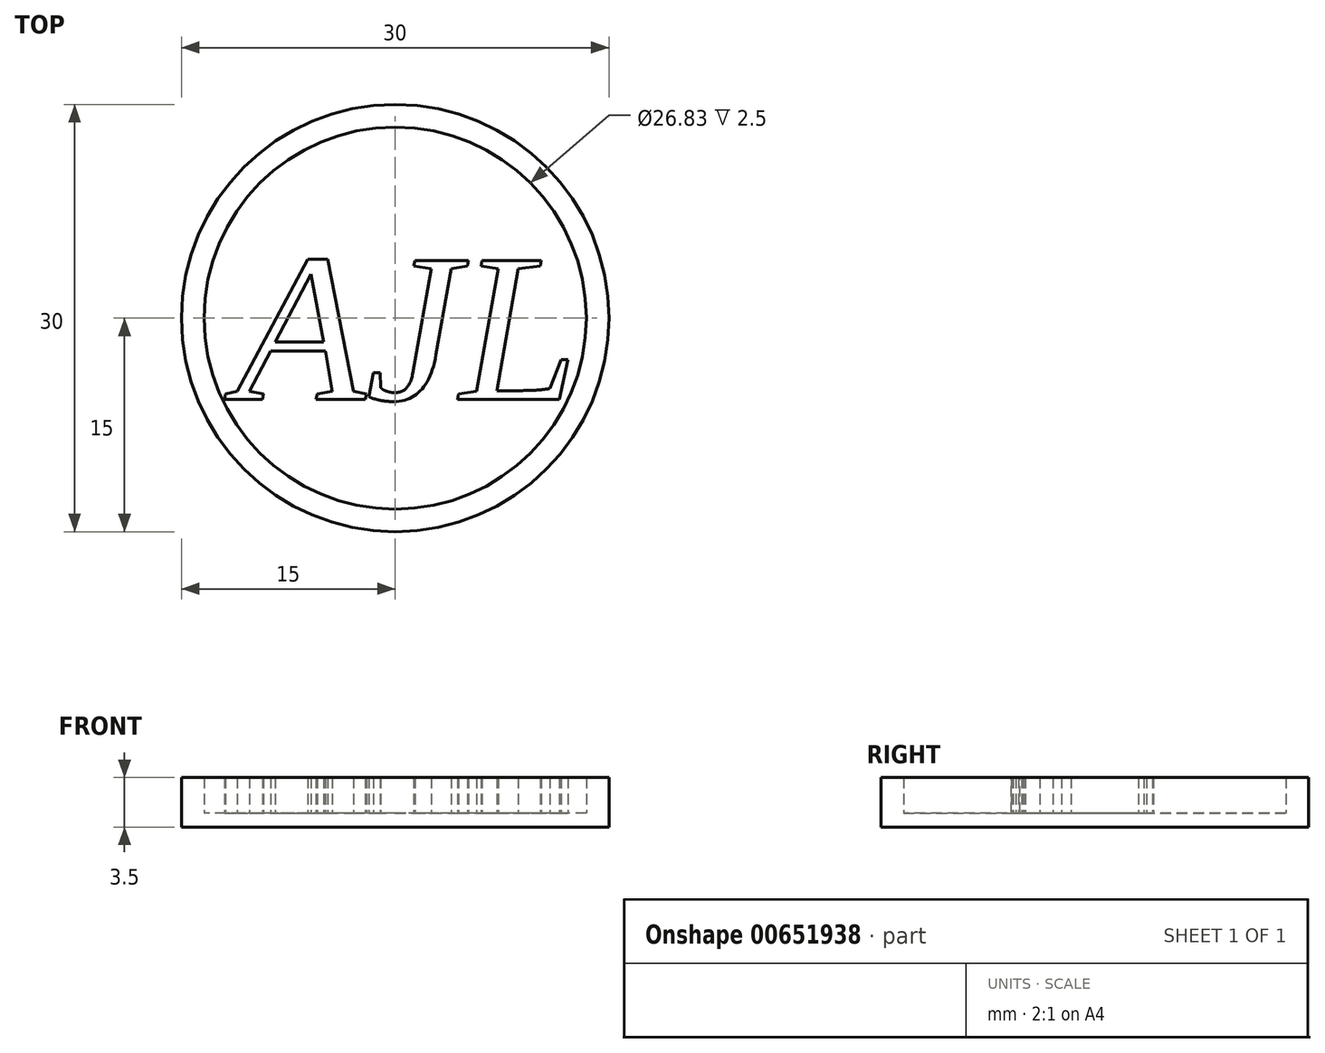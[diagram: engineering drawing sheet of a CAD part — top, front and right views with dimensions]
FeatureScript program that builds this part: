
annotation { "Feature Type Name" : "Feature", "Feature Type Description" : "" }
export const myFeature = defineFeature(function(context is Context, id is Id, definition is map)
    precondition{}
    {
        {
            var Q0;
            Q0=qCreatedBy(makeId("Top.planeOp"),FACE);
            var sketch = newSketch(context, id + "F0", { "sketchPlane" : qUnion([Q0])});
            skCircle(sketch, "E0", {"center": v(0, 0) * mm, "radius": 15 * mm});
            skSolve(sketch);
        }
        {
            var Q0;
            Q0=makeQuery(id+"F0.imprint","IMPRINT",FACE,{"disambiguationData":[TD([[makeQuery(id+"F0.imprint","IMPRINT",EDGE,{"derivedFrom":sQuery(id+"F0.wireOp",EDGE,"E0")}),1.0]])]});
            extrude(context, id + "F1", {"entities" : qUnion([Q0]), "depth" : 1 * mm, "offsetDistance" : 25 * mm});
        }
        {
            var Q0;
            Q0=makeQuery(id+"F1.opExtrude","CAP_FACE",FACE,{"disambiguationData":[OSD([sQuery(id+"F0.wireOp",EDGE,"E0")])],"isStart":false});
            var sketch = newSketch(context, id + "F2", { "sketchPlane" : qUnion([Q0])});
            skText(sketch, "E1", { "text": "AJL", "fontName": "Tinos-Italic.ttf"});
            const initialGuessF2  = {"E1": [-0.01117, -0.00572, 1, 0, 0.01073]};
            skSetInitialGuess(sketch, initialGuessF2);
            skSolve(sketch);
        }
        {
            var Q0;
            Q0 = qSketchRegion(id + "F2", true);
            extrude(context, id + "F3", {"entities" : qUnion([Q0]), "operationType" : NewBodyOperationType.ADD, "depth" : 2.5 * mm, "offsetDistance" : 25 * mm});
        }
        {
            var Q0;
            {var subQ0=sQuery(id+"F0.wireOp",EDGE,"E0");Q0=makeQuery(id+"F3.boolean.opBoolean","SPLIT",FACE,{"disambiguationData":[TD([makeQuery(id+"F1.opExtrude","SWEPT_FACE",FACE,{"disambiguationData":[OSD([subQ0])]})])],"derivedFrom":makeQuery(id+"F1.opExtrude","CAP_FACE",FACE,{"disambiguationData":[OSD([subQ0])],"isStart":false})});}
            var sketch = newSketch(context, id + "F4", { "sketchPlane" : qUnion([Q0])});
            skCircle(sketch, "E2", {"center": v(0, 0) * mm, "radius": 13.41 * mm});
            skCircle(sketch, "E3", {"center": v(0, 0) * mm, "radius": 15 * mm});
            skSolve(sketch);
        }
        {
            var Q0;
            Q0=makeQuery(id+"F4.imprint","IMPRINT",FACE,{"disambiguationData":[TD([[makeQuery(id+"F4.imprint","IMPRINT",EDGE,{"derivedFrom":sQuery(id+"F4.wireOp",EDGE,"E2")}),-1.0]])]});
            extrude(context, id + "F5", {"entities" : qUnion([Q0]), "operationType" : NewBodyOperationType.ADD, "depth" : 2.5 * mm, "offsetDistance" : 25 * mm});
        }
    });
